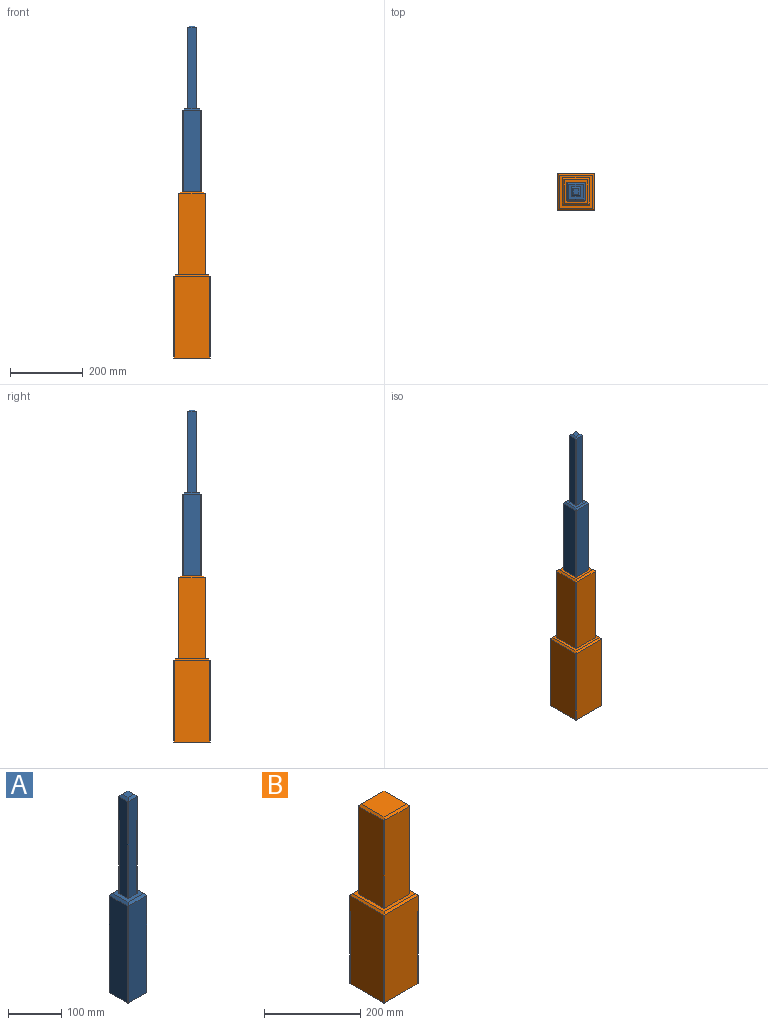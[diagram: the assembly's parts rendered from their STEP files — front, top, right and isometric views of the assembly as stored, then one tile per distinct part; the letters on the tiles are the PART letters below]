
ASSEMBLY  parts=2 mates=1
PART A: 27 faces, bbox 50.8x50.8x457.2 mm
  f0: plane 40.64x40.64mm, normal (0,0,1), area 1008.4mm2, adj f6,f7,f8,f9,f15,f16,f17,f18
  f1: plane 223.52x47.75mm, normal (1,0,0), area 10673.5mm2, adj f5,f15,f21,f22
  f2: plane 223.52x47.75mm, normal (0,1,0), area 10673.5mm2, adj f5,f16,f21,f23
  f3: plane 223.52x47.75mm, normal (-1,0,0), area 10673.5mm2, adj f5,f18,f23,f24
  f4: plane 223.52x47.75mm, normal (0,-1,0), area 10673.5mm2, adj f5,f17,f22,f24
  f5: plane 50.8x50.8mm, normal (0,0,-1), area 2578.6mm2, adj f1,f2,f3,f4,f21,f22,f23,f24
  f6: plane 223.52x22.35mm, normal (1,0,0), area 4996.1mm2, adj f0,f12,f20,f25
  f7: plane 223.52x22.35mm, normal (0,1,0), area 4996.1mm2, adj f0,f14,f25,f26
  f8: plane 223.52x22.35mm, normal (-1,0,0), area 4996.1mm2, adj f0,f13,f19,f26
  f9: plane 223.52x22.35mm, normal (0,-1,0), area 4996.1mm2, adj f0,f11,f19,f20
  f10: plane 15.24x15.24mm, normal (0,0,1), area 232.3mm2, adj f11,f12,f13,f14
  f11: plane 24.51x5.08mm, normal (0,-0.71,0.71), area 145.3mm2, adj f9,f10,f12,f13,f19,f20
  f12: plane 24.51x5.08mm, normal (0.71,0,0.71), area 145.3mm2, adj f6,f10,f11,f14,f20,f25
  f13: plane 24.51x5.08mm, normal (-0.71,0,0.71), area 145.3mm2, adj f8,f10,f11,f14,f19,f26
  f14: plane 24.51x5.08mm, normal (0,0.71,0.71), area 145.3mm2, adj f7,f10,f12,f13,f25,f26
  f15: plane 49.91x5.08mm, normal (0.71,0,0.71), area 327.8mm2, adj f0,f1,f16,f17,f21,f22
  f16: plane 49.91x5.08mm, normal (0,0.71,0.71), area 327.8mm2, adj f0,f2,f15,f18,f21,f23
  f17: plane 49.91x5.08mm, normal (0,-0.71,0.71), area 327.8mm2, adj f0,f4,f15,f18,f22,f24
  f18: plane 49.91x5.08mm, normal (-0.71,0,0.71), area 327.8mm2, adj f0,f3,f16,f17,f23,f24
  f19: cylinder r=1.52mm len=223.97mm, axis (0,0,1), area 535.4mm2, adj f0,f8,f9,f11,f13
  f20: cylinder r=1.52mm len=223.97mm, axis (0,0,-1), area 535.4mm2, adj f0,f6,f9,f11,f12
  f21: cylinder r=1.52mm len=223.97mm, axis (0,0,1), area 535.4mm2, adj f1,f2,f5,f15,f16
  f22: cylinder r=1.52mm len=223.97mm, axis (0,0,-1), area 535.4mm2, adj f1,f4,f5,f15,f17
  f23: cylinder r=1.52mm len=223.97mm, axis (0,0,-1), area 535.4mm2, adj f2,f3,f5,f16,f18
  f24: cylinder r=1.52mm len=223.97mm, axis (0,0,1), area 535.4mm2, adj f3,f4,f5,f17,f18
  f25: cylinder r=1.52mm len=223.97mm, axis (0,0,1), area 535.4mm2, adj f0,f6,f7,f12,f14
  f26: cylinder r=1.52mm len=223.97mm, axis (0,0,-1), area 535.4mm2, adj f0,f7,f8,f13,f14
PART B: 27 faces, bbox 101.6x101.6x457.2 mm
  f0: plane 223.52x98.55mm, normal (0,-1,0), area 22028.3mm2, adj f3,f15,f19,f20
  f1: plane 223.52x98.55mm, normal (1,0,0), area 22028.3mm2, adj f3,f16,f20,f21
  f2: plane 91.44x91.44mm, normal (0,0,1), area 2556.8mm2, adj f6,f7,f8,f9,f15,f16,f17,f18
  f3: plane 101.6x101.6mm, normal (0,0,-1), area 10320.6mm2, adj f0,f1,f4,f5,f19,f20,f21,f22
  f4: plane 223.52x98.55mm, normal (0,1,0), area 22028.3mm2, adj f3,f18,f21,f22
  f5: plane 223.52x98.55mm, normal (-1,0,0), area 22028.3mm2, adj f3,f17,f19,f22
  f6: plane 223.52x73.15mm, normal (0,1,0), area 16350.9mm2, adj f2,f13,f24,f25
  f7: plane 223.52x73.15mm, normal (-1,0,0), area 16350.9mm2, adj f2,f14,f25,f26
  f8: plane 223.52x73.15mm, normal (0,-1,0), area 16350.9mm2, adj f2,f12,f23,f26
  f9: plane 223.52x73.15mm, normal (1,0,0), area 16350.9mm2, adj f2,f11,f23,f24
  f10: plane 66.04x66.04mm, normal (0,0,1), area 4361.3mm2, adj f11,f12,f13,f14
  f11: plane 75.31x5.08mm, normal (0.71,0,0.71), area 510.2mm2, adj f9,f10,f12,f13,f23,f24
  f12: plane 75.31x5.08mm, normal (0,-0.71,0.71), area 510.2mm2, adj f8,f10,f11,f14,f23,f26
  f13: plane 75.31x5.08mm, normal (0,0.71,0.71), area 510.2mm2, adj f6,f10,f11,f14,f24,f25
  f14: plane 75.31x5.08mm, normal (-0.71,0,0.71), area 510.2mm2, adj f7,f10,f12,f13,f25,f26
  f15: plane 100.71x5.08mm, normal (0,-0.71,0.71), area 692.7mm2, adj f0,f2,f16,f17,f19,f20
  f16: plane 100.71x5.08mm, normal (0.71,0,0.71), area 692.7mm2, adj f1,f2,f15,f18,f20,f21
  f17: plane 100.71x5.08mm, normal (-0.71,0,0.71), area 692.7mm2, adj f2,f5,f15,f18,f19,f22
  f18: plane 100.71x5.08mm, normal (0,0.71,0.71), area 692.7mm2, adj f2,f4,f16,f17,f21,f22
  f19: cylinder r=1.52mm len=223.97mm, axis (0,0,-1), area 535.4mm2, adj f0,f3,f5,f15,f17
  f20: cylinder r=1.52mm len=223.97mm, axis (0,0,1), area 535.4mm2, adj f0,f1,f3,f15,f16
  f21: cylinder r=1.52mm len=223.97mm, axis (0,0,-1), area 535.4mm2, adj f1,f3,f4,f16,f18
  f22: cylinder r=1.52mm len=223.97mm, axis (0,0,1), area 535.4mm2, adj f3,f4,f5,f17,f18
  f23: cylinder r=1.52mm len=223.97mm, axis (0,0,1), area 535.4mm2, adj f2,f8,f9,f11,f12
  f24: cylinder r=1.52mm len=223.97mm, axis (0,0,-1), area 535.4mm2, adj f2,f6,f9,f11,f13
  f25: cylinder r=1.52mm len=223.97mm, axis (0,0,1), area 535.4mm2, adj f2,f6,f7,f13,f14
  f26: cylinder r=1.52mm len=223.97mm, axis (0,0,-1), area 535.4mm2, adj f2,f7,f8,f12,f14
PLACE A t=(0,0,457.2)mm
PLACE B at identity
MATE fastened B.f10 <-> A.f5  axis (0,0,1) through (0,0,457.2)mm
